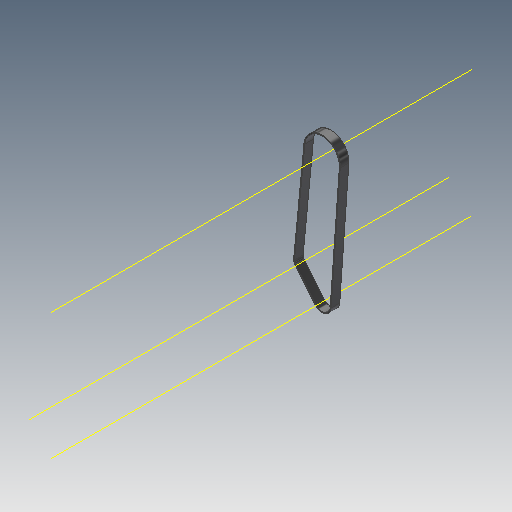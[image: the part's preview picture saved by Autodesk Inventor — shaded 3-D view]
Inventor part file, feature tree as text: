
AUTODESK INVENTOR PART (.ipt)
format: ipt  version: 2018 (Build 220112000, 112)  size: 105,472 bytes
history: native  units: mm (DEFAULTED — no unit token found)
features: other x5, plane x3, sketch x1, sweep x1
ambient origin geometry x8: Origin, YZ Plane, XZ Plane, XY Plane, X Axis, Y Axis, Z Axis, Center Point
bodies: Solid1 (feature_tree)
feature tree (10):
  sketch  "Sketch Path"  dims[d0=6.0mm d2=0.0mm d4=0.3mm d5=0.3mm d6=0.0mm d7=0.0mm d8=0.0mm d9=0.0mm d10=0.0mm d11=0.0mm d12=0.0mm d13=0.0mm]
  other  "Cross Section Plane"
  other  "Work Axis1"
  other  "Work Axis2"
  other  "Work Axis3"
  plane  "Work Plane2"
  plane  "Work Plane3"
  plane  "Work Plane4"
  sweep  "Belt"
  other  "Cross Section"
